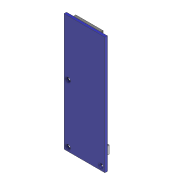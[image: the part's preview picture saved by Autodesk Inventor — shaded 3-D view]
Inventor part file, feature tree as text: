
AUTODESK INVENTOR PART (.ipt)
format: ipt  version: 2022.3 (Build 263350000, 350)  size: 193,536 bytes
history: native  units: mm
features: extrude x9, sketch x9, other x1
ambient origin geometry x8: Origin, YZ Plane, XZ Plane, XY Plane, X Axis, Y Axis, Z Axis, Center Point
bodies: Body1 (feature_tree)
feature tree (19):
  other  "Sólido1"
  extrude  "Extrusión1"  Depth=75.3mm
  extrude  "Extrusión2"  Depth=2.5mm
  extrude  "Extrusión3"  Depth=3.0mm
  extrude  "Extrusión4"  Depth=3.0mm
  extrude  "Extrusión5"  Depth=1.6mm TaperAngle=0.0deg
  extrude  "Extrusión6"  Depth=2.5mm TaperAngle=0.0deg
  extrude  "Extrusión7"  Depth=1.0mm TaperAngle=0.0deg
  extrude  "Extrusión8"  Depth=3.0mm TaperAngle=0.0deg
  extrude  "Extrusión9"  Depth=0.1mm TaperAngle=0.0deg
  sketch  "Boceto1"  dims[d0=26.25mm d1=75.3mm]
  sketch  "Boceto3"  dims[d2=2.5mm d3=10.5mm]
  sketch  "Boceto4"  dims[d4=21.0mm d5=3.0mm]
  sketch  "Boceto5"  dims[d6=3.0mm d7=37.3mm]
  sketch  "Boceto6"  dims[d8=3.0mm d9=1.6mm d10=0.0mm]
  sketch  "Boceto7"  dims[d11=1.6mm d12=0.0mm d13=2.5mm d14=0.0mm]
  sketch  "Boceto8"  dims[d15=0.1mm d16=0.0mm d17=1.0mm d18=0.0mm]
  sketch  "Boceto9"  dims[d19=5.5mm d20=0.0mm d21=3.0mm d22=0.0mm]
  sketch  "Boceto10"  dims[d23=0.1mm d24=0.0mm d25=0.1mm d26=0.0mm]
